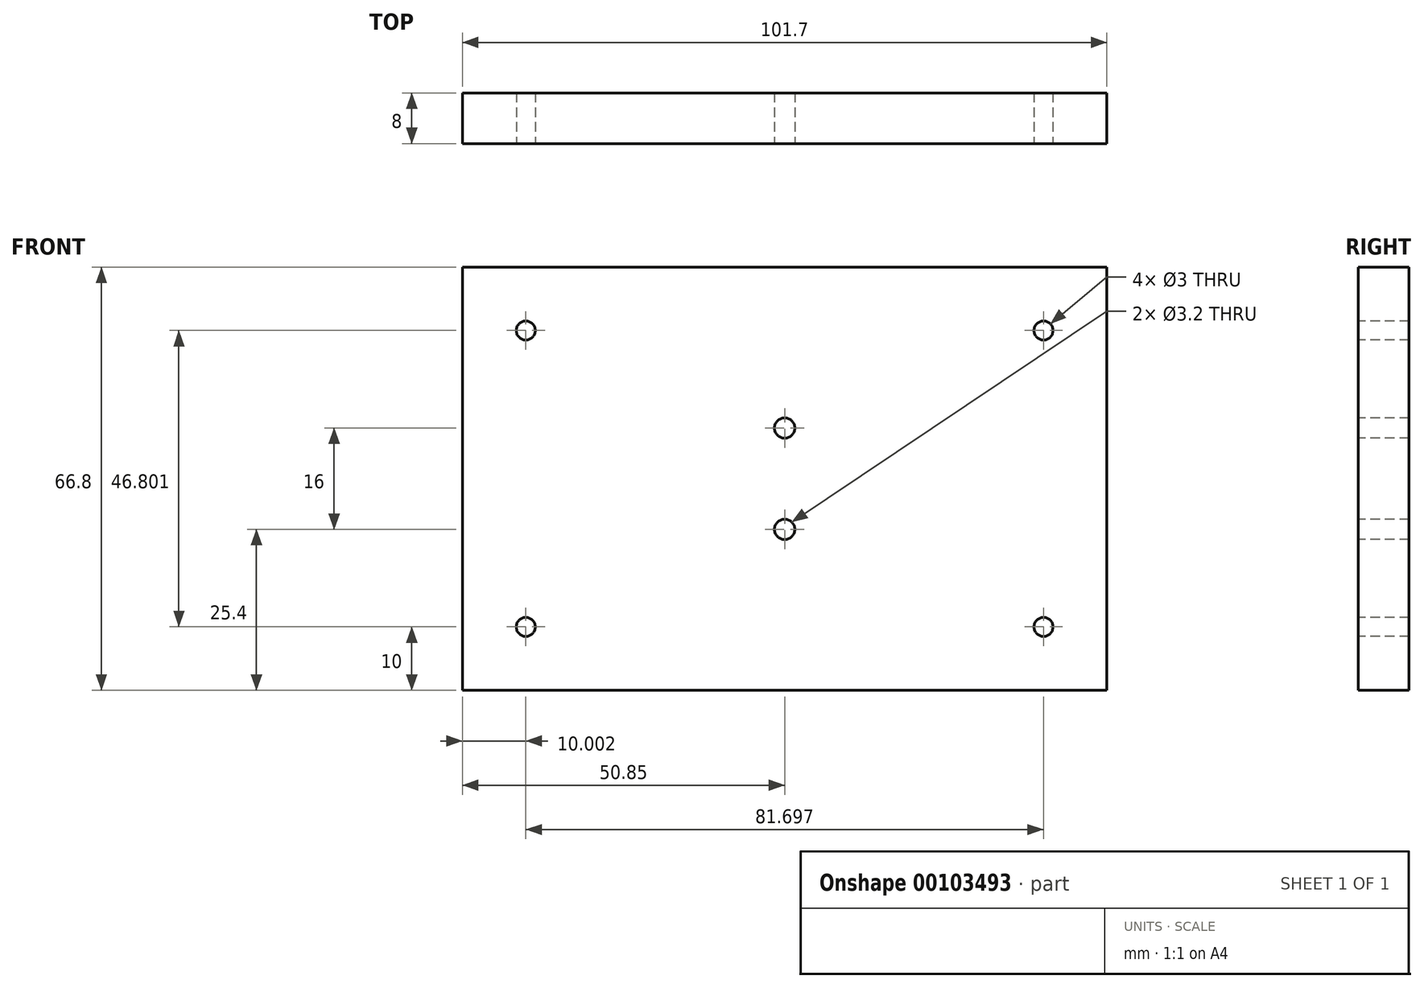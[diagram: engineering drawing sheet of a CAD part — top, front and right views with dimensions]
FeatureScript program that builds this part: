
annotation { "Feature Type Name" : "Feature", "Feature Type Description" : "" }
export const myFeature = defineFeature(function(context is Context, id is Id, definition is map)
    precondition{}
    {
        {
            var Q0;
            Q0=qCreatedBy(makeId("Front.planeOp"),FACE);
            var sketch = newSketch(context, id + "F0", { "sketchPlane" : qUnion([Q0])});
            skLineSegment(sketch, "E0.bottom", {"start": v(50.85, -33.4) * mm, "end": v(-50.85, -33.4) * mm});
            skLineSegment(sketch, "E0.top", {"start": v(50.85, 33.4) * mm, "end": v(-50.85, 33.4) * mm});
            skLineSegment(sketch, "E0.left", {"start": v(50.85, -33.4) * mm, "end": v(50.85, 33.4) * mm});
            skLineSegment(sketch, "E0.right", {"start": v(-50.85, -33.4) * mm, "end": v(-50.85, 33.4) * mm});
            skPoint(sketch, "E0.middle", {"position": v(0, 0) * mm});
            skSolve(sketch);
        }
        {
            var Q0;
            Q0 = qSketchRegion(id + "F0", true);
            extrude(context, id + "F1", {"entities" : qUnion([Q0]), "endBound" : BoundingType.SYMMETRIC, "depth" : 8 * mm});
        }
        {
            var Q0;
            Q0=makeQuery(id+"F1.opExtrude","CAP_FACE",FACE,{"disambiguationData":[OSD([sQuery(id+"F0.wireOp",EDGE,"E0.bottom"),sQuery(id+"F0.wireOp",EDGE,"E0.top"),sQuery(id+"F0.wireOp",EDGE,"E0.left"),sQuery(id+"F0.wireOp",EDGE,"E0.right")])],"isStart":false});
            var sketch = newSketch(context, id + "F2", { "sketchPlane" : qUnion([Q0])});
            skCircle(sketch, "E1", {"center": v(-40.85, 23.4) * mm, "radius": 1.5 * mm});
            skCircle(sketch, "E2.MirrorC", {"center": v(40.85, 23.4) * mm, "radius": 1.5 * mm});
            skCircle(sketch, "E3.MirrorC", {"center": v(40.85, -23.4) * mm, "radius": 1.5 * mm});
            skCircle(sketch, "E4.MirrorC", {"center": v(-40.85, -23.4) * mm, "radius": 1.5 * mm});
            skPoint(sketch, "E5", {"position": v(0, 8) * mm});
            skPoint(sketch, "E6.MirrorP", {"position": v(0, -8) * mm});
            skSolve(sketch);
        }
        {
            var Q0;
            Q0=sQuery(id+"F2.wireOp",VERTEX,"E1.center");
            var Q1;
            Q1=sQuery(id+"F2.wireOp",VERTEX,"E2.MirrorC.center");
            var Q2;
            Q2=sQuery(id+"F2.wireOp",VERTEX,"E3.MirrorC.center");
            var Q3;
            Q3=sQuery(id+"F2.wireOp",VERTEX,"E4.MirrorC.center");
            var Q4;
            Q4=makeQuery(id+"F1.opExtrude","SWEPT_BODY",BODY,{"disambiguationData":[OSD([sQuery(id+"F0.wireOp",EDGE,"E0.bottom"),sQuery(id+"F0.wireOp",EDGE,"E0.top"),sQuery(id+"F0.wireOp",EDGE,"E0.left"),sQuery(id+"F0.wireOp",EDGE,"E0.right")])]});
            hole(context, id + "F3", {"style" : HoleStyle.SIMPLE, "endStyle" : HoleEndStyle.THROUGH, "holeDiameter" : 3 * mm, "locations" : qUnion([Q0, Q1, Q2, Q3]), "scope" : qUnion([Q4]), "isTappedThrough" : true});
        }
        {
            var Q0;
            Q0=sQuery(id+"F2.wireOp",VERTEX,"E5");
            var Q1;
            Q1=sQuery(id+"F2.wireOp",VERTEX,"E6.MirrorP");
            var Q2;
            Q2=makeQuery(id+"F1.opExtrude","SWEPT_BODY",BODY,{"disambiguationData":[OSD([sQuery(id+"F0.wireOp",EDGE,"E0.bottom"),sQuery(id+"F0.wireOp",EDGE,"E0.top"),sQuery(id+"F0.wireOp",EDGE,"E0.left"),sQuery(id+"F0.wireOp",EDGE,"E0.right")])]});
            hole(context, id + "F4", {"style" : HoleStyle.SIMPLE, "endStyle" : HoleEndStyle.THROUGH, "holeDiameter" : 3.2 * mm, "locations" : qUnion([Q0, Q1]), "scope" : qUnion([Q2]), "isTappedThrough" : true});
        }
    });
